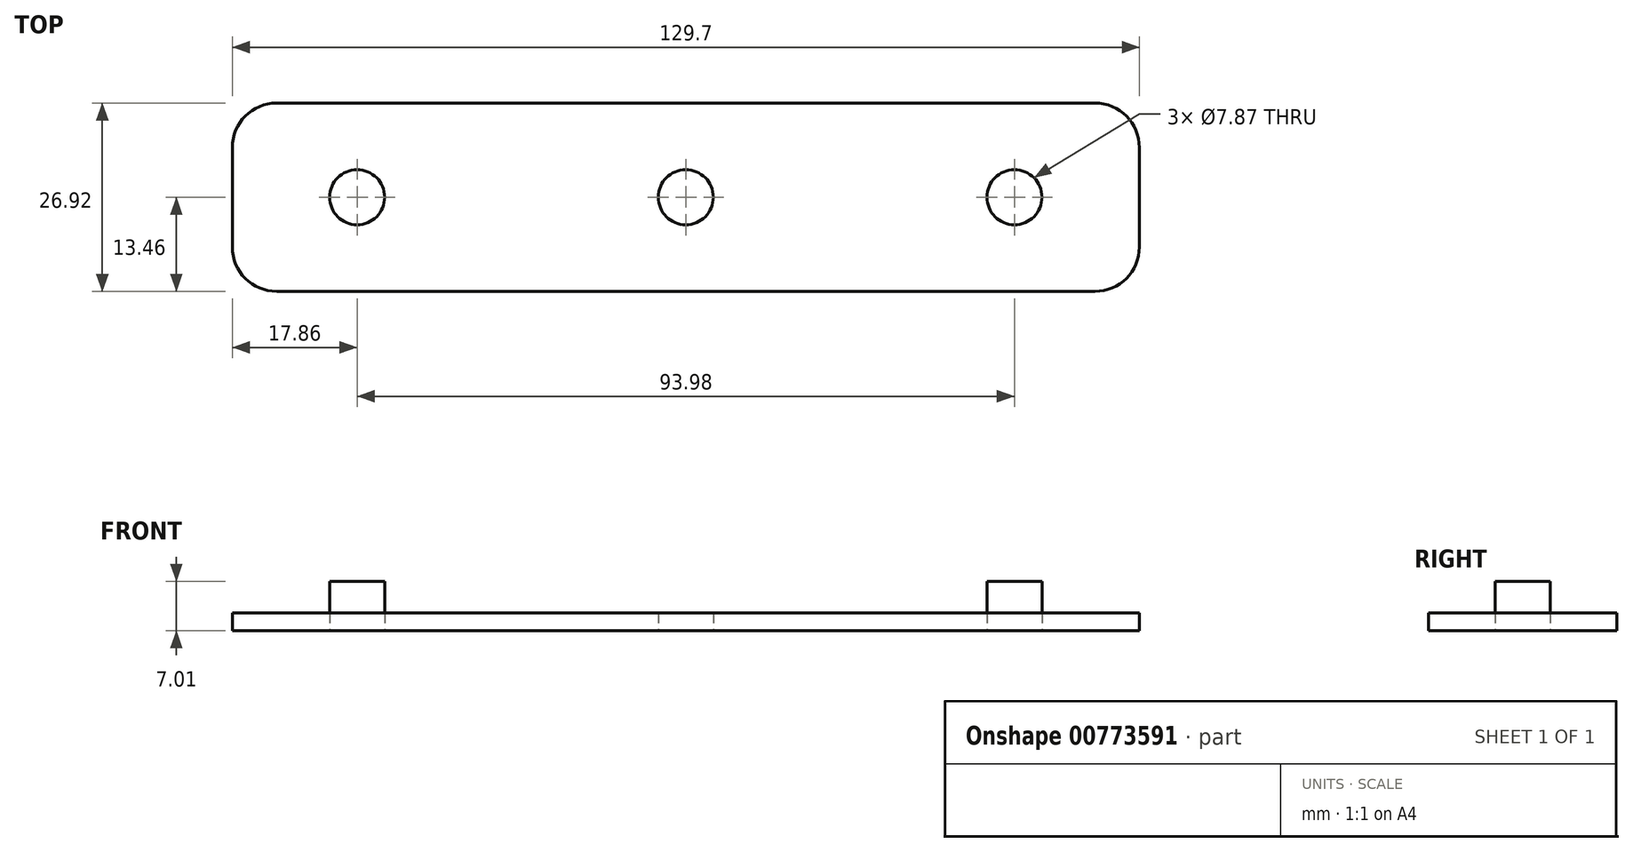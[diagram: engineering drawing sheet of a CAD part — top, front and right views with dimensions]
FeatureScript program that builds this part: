
annotation { "Feature Type Name" : "Feature", "Feature Type Description" : "" }
export const myFeature = defineFeature(function(context is Context, id is Id, definition is map)
    precondition{}
    {
        {
            var Q0;
            Q0=qCreatedBy(makeId("Top.planeOp"),FACE);
            var sketch = newSketch(context, id + "F0", { "sketchPlane" : qUnion([Q0])});
            skCircle(sketch, "E0", {"center": v(0, 0) * mm, "radius": 3.94 * mm});
            skLineSegment(sketch, "E1", {"start": v(0, 0) * mm, "end": v(47, 0) * mm});
            skCircle(sketch, "E2", {"center": v(47, 0) * mm, "radius": 3.94 * mm});
            skLineSegment(sketch, "E3", {"start": v(0, 0) * mm, "end": v(-47, 0) * mm});
            skCircle(sketch, "E4", {"center": v(-47, 0) * mm, "radius": 3.94 * mm});
            skLineSegment(sketch, "E5", {"start": v(0, 3.94) * mm, "end": v(0, 13.46) * mm});
            skLineSegment(sketch, "E6", {"start": v(0, -3.94) * mm, "end": v(0, -13.46) * mm});
            skLineSegment(sketch, "E7", {"start": v(-50.93, 0) * mm, "end": v(-64.85, 0) * mm});
            skLineSegment(sketch, "E8", {"start": v(50.93, 0) * mm, "end": v(64.85, 0) * mm});
            skLineSegment(sketch, "E9", {"start": v(-58.5, 13.46) * mm, "end": v(58.5, 13.46) * mm});
            skLineSegment(sketch, "E10", {"start": v(64.85, 7.11) * mm, "end": v(64.85, -7.11) * mm});
            skLineSegment(sketch, "E11", {"start": v(58.5, -13.46) * mm, "end": v(-58.5, -13.46) * mm});
            skLineSegment(sketch, "E12", {"start": v(-64.85, -7.11) * mm, "end": v(-64.85, 7.11) * mm});
            skPoint(sketch, "E13.visualSharp", {"position": v(-64.85, 13.46) * mm});
            skArc(sketch, "E13.filletArc", {"start": v(-58.5, 13.46) * mm, "mid": v(-62.99, 11.6) * mm, "end": v(-64.85, 7.11) * mm});
            skPoint(sketch, "E14.visualSharp", {"position": v(-64.85, -13.46) * mm});
            skArc(sketch, "E14.filletArc", {"start": v(-64.85, -7.11) * mm, "mid": v(-62.99, -11.6) * mm, "end": v(-58.5, -13.46) * mm});
            skPoint(sketch, "E15.visualSharp", {"position": v(64.85, 13.46) * mm});
            skArc(sketch, "E15.filletArc", {"start": v(64.85, 7.11) * mm, "mid": v(62.99, 11.6) * mm, "end": v(58.5, 13.46) * mm});
            skPoint(sketch, "E16.visualSharp", {"position": v(64.85, -13.46) * mm});
            skArc(sketch, "E16.filletArc", {"start": v(58.5, -13.46) * mm, "mid": v(62.99, -11.6) * mm, "end": v(64.85, -7.11) * mm});
            skSolve(sketch);
        }
        {
            var Q0;
            {var subQ0=sQuery(id+"F0.wireOp",EDGE,"E2");var subQ1=makeQuery(id+"F0.imprint","INTERSECT",VERTEX,{"derivedFrom":[subQ0,sQuery(id+"F0.wireOp",EDGE,"E8")]});Q0=makeQuery(id+"F0.imprint","IMPRINT",FACE,{"disambiguationData":[TD([[makeQuery(id+"F0.imprint","IMPRINT",EDGE,{"disambiguationData":[TD([[subQ1,-1.0]])],"derivedFrom":subQ0}),1.0]])]});}
            var Q1;
            {var subQ0=sQuery(id+"F0.wireOp",EDGE,"E4");var subQ1=makeQuery(id+"F0.imprint","INTERSECT",VERTEX,{"derivedFrom":[subQ0,sQuery(id+"F0.wireOp",EDGE,"E7")]});Q1=makeQuery(id+"F0.imprint","IMPRINT",FACE,{"disambiguationData":[TD([[makeQuery(id+"F0.imprint","IMPRINT",EDGE,{"disambiguationData":[TD([[subQ1,1.0]])],"derivedFrom":subQ0}),1.0]])]});}
            extrude(context, id + "F1", {"entities" : qUnion([Q0, Q1]), "depth" : 7 * mm, "offsetDistance" : 25.4 * mm});
        }
        {
            var Q0;
            Q0 = qSketchRegion(id + "F0", true);
            extrude(context, id + "F2", {"entities" : qUnion([Q0]), "depth" : 2.54 * mm, "offsetDistance" : 25.4 * mm});
        }
    });
